# Revit family: Ventüer_AcousticLouvres_AL-100W
name_source: partatom
category: Generic Models
units: mm (PartAtom-declared; Revit-internal decimal feet)

## family parameters
Always vertical = No
Can host rebar = No
Cut with Voids When Loaded = Yes
Part Type = Normal
Room Calculation Point = No
Round Connector Dimension = Use Diameter
Shared = No
Work Plane-Based = Yes

## types (1)
- AL-100W
    Ancillaries = Bird Mesh, Insect Mesh, Solid Blanking, Perimeter Mounting Angle
    Base Width = 52 mm
    Blade And Frame Gap = 10 mm  [stored 0.0328084 ft]
    Blade Centres = 150 mm
    Blade Count = 3
    Blade Cut Offset = 450 mm  [stored 1.47638 ft]
    Blade Horizontal Offset = 6 mm  [stored 0.019685 ft]
    Blade Material = Ventüer Aluminium
    Connector Height = 490 mm  [stored 1.60761 ft]
    Connector Width = 490 mm  [stored 1.60761 ft]
    Default Elevation = 1219 mm
    Depth = 101 mm
    Description = 100mm Acoustic Weather Louvre
    Exact Neck Height = 594 mm  [stored 1.94882 ft]
    Exact Neck Height Check = 594 mm  [stored 1.94882 ft]
    Exact Neck Width = 594 mm  [stored 1.94882 ft]
    Exact Neck Width Check = 594 mm  [stored 1.94882 ft]
    Fill Material = Ventüer Insulation
    Frame Material = Ventüer Aluminium
    Frame Set Count = 1
    Frame Set Count Check = 2
    Frame Set Transition Count = 1
    Frame Set Transition Count Check = 2
    Frame Set Width = 490 mm  [stored 1.60761 ft]
    Keynote = AL-100W
    Manufacturer = Ventüer
    Max Flow = 5000.0 L/s
    Min Flow = 100.0 L/s
    Model = AL-100W
    Multiple Frame Set = No
    Multiple Transition = No
    Noise Level NC Max = 0.00 NC
    Noise Level NC Min = 0.00 NC
    Nominal Height = 600 mm
    Nominal Width = 600 mm
    Nominated Air Flow = 100.0 L/s
    Nominated Pessure Drop = 21.0 Pa
    Overall Opening Height = 490 mm  [stored 1.60761 ft]
    Overall Opening Width = 490 mm  [stored 1.60761 ft]
    Profile Width = 52 mm
    Screen Symbol Distance = 6 mm  [stored 0.019685 ft]
    Siffener Length = 490 mm  [stored 1.60761 ft]
    Single Frame Set = Yes
    Single Frame Set Width = 245 mm  [stored 0.803806 ft]
    Single Transition = No
    Specified Air Flow = 0.0 L/s
    Specified Pressure Drop = 21.0 Pa
    Static Pressure Max = 60.0 Pa
    Static Pressure Min = 10.0 Pa
    Top Blade Corrector = 0 mm  [stored 0 ft]
    Top Blade Height = 30 mm  [stored 0.0984252 ft]
    URL = https://www.ventuer.co
    Ventüer Product Range = Acoustic Louvres

note: [stored X ft] marks values corroborated as IEEE doubles in the binary element streams (Revit-internal decimal feet)

## geometry (parser evidence)
native form markers: Sweep x27
no freeform markers — native parametric forms only
